# Revit family: Legrand Cabinet XL³ 800 Metal
name_source: partatom
category: Equipement électrique
units: mm (PartAtom-declared; Revit-internal decimal feet)

## family parameters
Basée sur le plan de construction = Non
Configuration du panneau = Deux colonnes, circuits au sein
Cote de connecteur circulaire = Utiliser le diamètre
Couper avec des vides une fois chargée = Non
Numéro OmniClass = 23.80.30.11.17
Partagée = Non
Point de calcul de pièce = Non
Titre OmniClass = Distribution Boards and Control Panels
Toujours verticalement = Oui
Type d'élément = Tableau de raccordement

## types (8) — shared parameters
Fabricant = Legrand
Finish = Epoxipolyester paint deposited by electrostatic powder
General Conditions of Use = https://export.legrand.com
ICW (until) (kA) = 25
IK with door = 08
IK without door = 07
IN max (A) = 800
IP with door = 43
IP without door = 30
IPK (kA) = 50
Material = Steel
Material corner = Plastic
Modèle = XL³ 800
RAL = 7035
URL = https://www.legrand.fr
depth (mm) = 230 mm  [stored 0.754593 ft]
depth installation zone = 1330 mm  [stored 4.36352 ft]
width installation zone = 2360 mm  [stored 7.74278 ft]
zero-valued in all types: Elévation par défaut

## per-type parameters (varying)
| type | Cabinets | Enclosures | height | height installation zone | height total (mm) | level Cabinet | level installation zone | width (mm) |
| 020401-021251 | Oui | Non | 1050 mm | 1050 mm | 1050 mm | 0 mm  [stored 0 ft] | 5 mm  [stored 0.0164042 ft] | 660 mm |
| 020404-021254 | Non | Oui | 1850 mm  [stored 6.06955 ft] | 1950 mm  [stored 6.39764 ft] | 1950 mm  [stored 6.39764 ft] | 100 mm  [stored 0.328084 ft] | 0 mm  [stored 0 ft] | 660 mm |
| 020402-021252 | Oui | Non | 1250 mm  [stored 4.10105 ft] | 1250 mm  [stored 4.10105 ft] | 1250 mm  [stored 4.10105 ft] | 0 mm  [stored 0 ft] | 5 mm  [stored 0.0164042 ft] | 660 mm |
| 020406-021256 | Oui | Non | 1050 mm | 1050 mm | 1050 mm | 0 mm  [stored 0 ft] | 5 mm  [stored 0.0164042 ft] | 910 mm |
| 020407-021257 | Oui | Non | 1250 mm  [stored 4.10105 ft] | 1250 mm  [stored 4.10105 ft] | 1250 mm  [stored 4.10105 ft] | 0 mm  [stored 0 ft] | 5 mm  [stored 0.0164042 ft] | 910 mm |
| 020403-021253 | Non | Oui | 1450 mm  [stored 4.75722 ft] | 1550 mm  [stored 5.0853 ft] | 1550 mm  [stored 5.0853 ft] | 100 mm  [stored 0.328084 ft] | 0 mm  [stored 0 ft] | 660 mm |
| 020408-021258 | Non | Oui | 1450 mm  [stored 4.75722 ft] | 1550 mm  [stored 5.0853 ft] | 1550 mm  [stored 5.0853 ft] | 100 mm  [stored 0.328084 ft] | 0 mm  [stored 0 ft] | 910 mm |
| 020409-021259 | Non | Oui | 1850 mm  [stored 6.06955 ft] | 1950 mm  [stored 6.39764 ft] | 1950 mm  [stored 6.39764 ft] | 100 mm  [stored 0.328084 ft] | 0 mm  [stored 0 ft] | 910 mm |

note: [stored X ft] marks values corroborated as IEEE doubles in the binary element streams (Revit-internal decimal feet)
